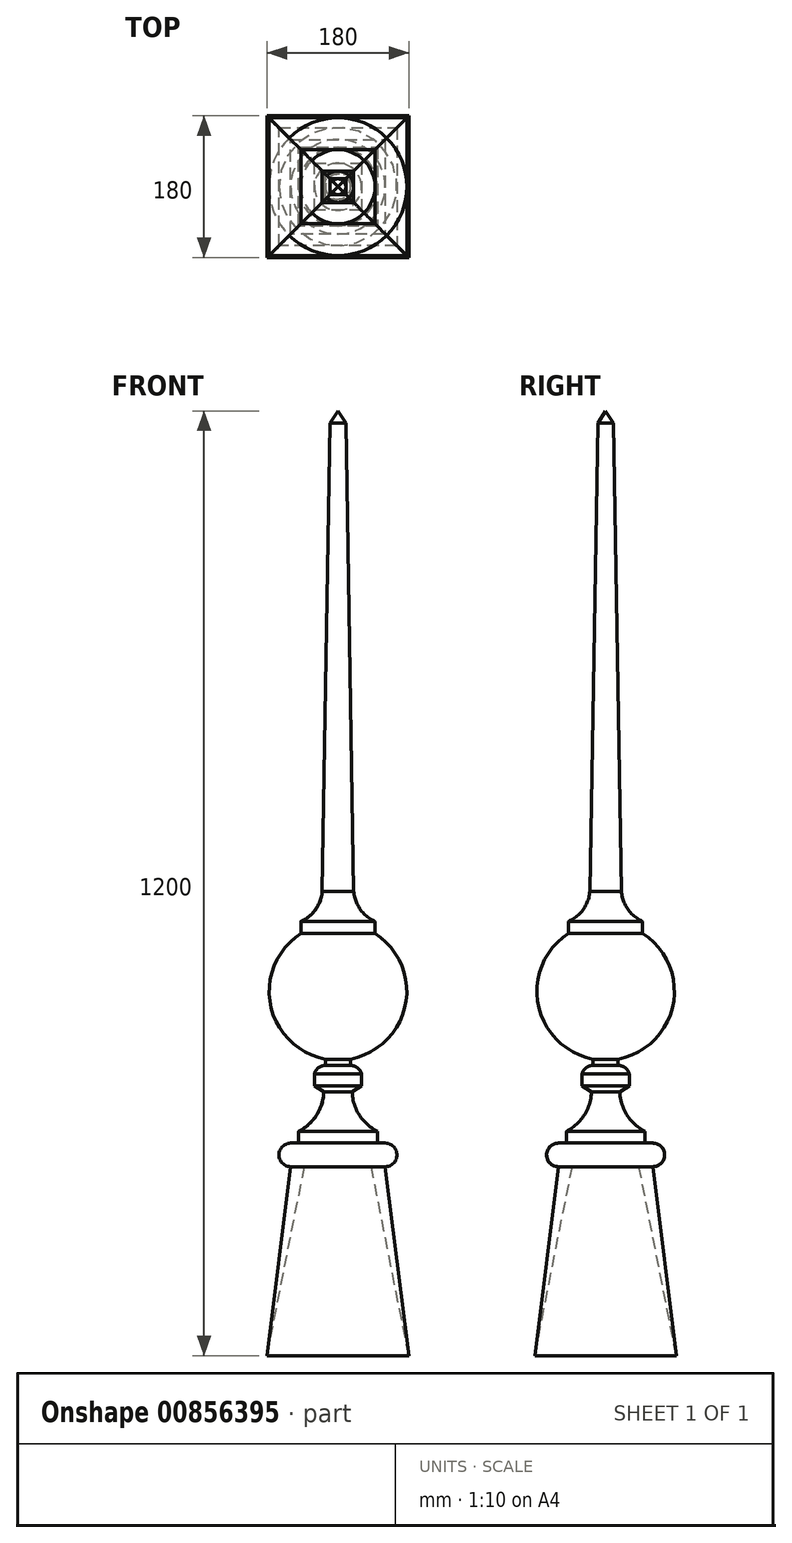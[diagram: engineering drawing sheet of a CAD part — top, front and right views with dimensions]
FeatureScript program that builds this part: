
annotation { "Feature Type Name" : "Feature", "Feature Type Description" : "" }
export const myFeature = defineFeature(function(context is Context, id is Id, definition is map)
    precondition{}
    {
        {
            var Q0;
            Q0=qCreatedBy(makeId("Front.planeOp"),FACE);
            var sketch = newSketch(context, id + "F0", { "sketchPlane" : qUnion([Q0])});
            skLineSegment(sketch, "E0", {"start": v(0, 0) * mm, "end": v(0, 1200) * mm});
            skPoint(sketch, "E1", {"position": v(0, 600) * mm});
            skLineSegment(sketch, "E2", {"start": v(0, 0) * mm, "end": v(90, 0) * mm});
            skLineSegment(sketch, "E3", {"start": v(90, 0) * mm, "end": v(60, 240) * mm});
            skLineSegment(sketch, "E4", {"start": v(60, 240) * mm, "end": v(0, 240) * mm});
            skLineSegment(sketch, "E5", {"start": v(0, 270) * mm, "end": v(60, 270) * mm});
            skArc(sketch, "E6", {"start": v(60, 240) * mm, "mid": v(75, 255) * mm, "end": v(60, 270) * mm});
            skLineSegment(sketch, "E7", {"start": v(50, 270) * mm, "end": v(50, 285) * mm});
            skLineSegment(sketch, "E8", {"start": v(50, 285) * mm, "end": v(0, 285) * mm, "construction": true});
            skLineSegment(sketch, "E9", {"start": v(0, 335) * mm, "end": v(18, 335) * mm, "construction": true});
            skLineSegment(sketch, "E10", {"start": v(18, 335) * mm, "end": v(30, 343) * mm});
            skLineSegment(sketch, "E11", {"start": v(30, 343) * mm, "end": v(30, 358) * mm});
            skLineSegment(sketch, "E12", {"start": v(0, 368.67) * mm, "end": v(16, 368.67) * mm, "construction": true});
            skLineSegment(sketch, "E13", {"start": v(16, 368.67) * mm, "end": v(16, 376.67) * mm});
            skLineSegment(sketch, "E14", {"start": v(16, 376.67) * mm, "end": v(0, 376.67) * mm, "construction": true});
            skArc(sketch, "E15", {"start": v(18, 335) * mm, "mid": v(27.1, 305.59) * mm, "end": v(50, 285) * mm});
            skArc(sketch, "E16", {"start": v(30, 358) * mm, "mid": v(24.8, 365.7) * mm, "end": v(16, 368.67) * mm});
            skLineSegment(sketch, "E17", {"start": v(0, 551.67) * mm, "end": v(46.98, 551.67) * mm});
            skLineSegment(sketch, "E18", {"start": v(46.98, 551.67) * mm, "end": v(46.98, 536.67) * mm});
            skLineSegment(sketch, "E19", {"start": v(46.98, 536.67) * mm, "end": v(0, 536.67) * mm});
            skArc(sketch, "E20", {"start": v(0, 550.33) * mm, "mid": v(-87.57, 462.76) * mm, "end": v(0, 375.2) * mm, "construction": true});
            skArc(sketch, "E21", {"start": v(0, 375.2) * mm, "mid": v(87.57, 462.76) * mm, "end": v(0, 550.33) * mm});
            skLineSegment(sketch, "E22", {"start": v(0, 590) * mm, "end": v(20, 590) * mm});
            skArc(sketch, "E23", {"start": v(20, 590) * mm, "mid": v(28.21, 567.12) * mm, "end": v(46.98, 551.67) * mm});
            skLineSegment(sketch, "E24", {"start": v(0, 1185) * mm, "end": v(10, 1185) * mm});
            skLineSegment(sketch, "E25", {"start": v(10, 1185) * mm, "end": v(20, 590) * mm});
            skLineSegment(sketch, "E26", {"start": v(0, 1200) * mm, "end": v(10, 1185) * mm});
            skSolve(sketch);
        }
        {
            var Q0;
            Q0=qCreatedBy(makeId("Top.planeOp"),FACE);
            var sketch = newSketch(context, id + "F1", { "sketchPlane" : qUnion([Q0])});
            skLineSegment(sketch, "E27.bottom", {"start": v(90, -90) * mm, "end": v(-90, -90) * mm});
            skLineSegment(sketch, "E27.top", {"start": v(90, 90) * mm, "end": v(-90, 90) * mm});
            skLineSegment(sketch, "E27.left", {"start": v(90, -90) * mm, "end": v(90, 90) * mm});
            skLineSegment(sketch, "E27.right", {"start": v(-90, -90) * mm, "end": v(-90, 90) * mm});
            skPoint(sketch, "E27.middle", {"position": v(0, 0) * mm});
            skSolve(sketch);
        }
        {
            var Q0;
            {var subQ0=sQuery(id+"F0.wireOp",EDGE,"E17");Q0=makeQuery(id+"F0.imprint","IMPRINT",FACE,{"disambiguationData":[TD([[makeQuery(id+"F0.imprint","IMPRINT",EDGE,{"derivedFrom":subQ0}),-1.0]])]});}
            var Q1;
            {var subQ5=sQuery(id+"F0.wireOp",EDGE,"E4");Q1=makeQuery(id+"F0.imprint","IMPRINT",FACE,{"disambiguationData":[TD([[makeQuery(id+"F0.imprint","IMPRINT",EDGE,{"derivedFrom":subQ5}),-1.0]])]});}
            var Q2;
            {var subQ2=sQuery(id+"F0.wireOp",EDGE,"E24");Q2=makeQuery(id+"F0.imprint","IMPRINT",FACE,{"disambiguationData":[TD([[makeQuery(id+"F0.imprint","IMPRINT",EDGE,{"derivedFrom":subQ2}),1.0]])]});}
            var Q3;
            {var subQ0=sQuery(id+"F0.wireOp",EDGE,"E19");Q3=makeQuery(id+"F0.imprint","IMPRINT",FACE,{"disambiguationData":[TD([[makeQuery(id+"F0.imprint","IMPRINT",EDGE,{"derivedFrom":subQ0}),-1.0]])]});}
            var Q4;
            {var subQ0=sQuery(id+"F0.wireOp",EDGE,"E22");Q4=makeQuery(id+"F0.imprint","IMPRINT",FACE,{"disambiguationData":[TD([[makeQuery(id+"F0.imprint","IMPRINT",EDGE,{"derivedFrom":subQ0}),1.0]])]});}
            var Q5;
            {var subQ0=sQuery(id+"F0.wireOp",EDGE,"E19");Q5=makeQuery(id+"F0.imprint","IMPRINT",FACE,{"disambiguationData":[TD([[makeQuery(id+"F0.imprint","IMPRINT",EDGE,{"derivedFrom":subQ0}),1.0]])]});}
            var Q6;
            {var subQ0=sQuery(id+"F0.wireOp",EDGE,"E17");Q6=makeQuery(id+"F0.imprint","IMPRINT",FACE,{"disambiguationData":[TD([[makeQuery(id+"F0.imprint","IMPRINT",EDGE,{"derivedFrom":subQ0}),1.0]])]});}
            var Q7;
            {var subQ0=sQuery(id+"F0.wireOp",EDGE,"E7");Q7=makeQuery(id+"F0.imprint","IMPRINT",FACE,{"disambiguationData":[TD([[makeQuery(id+"F0.imprint","IMPRINT",EDGE,{"derivedFrom":subQ0}),1.0]])]});}
            var Q8;
            Q8=sQuery(id+"F0.wireOp",EDGE,"E0");
            revolve(context, id + "F2", {"surfaceOperationType" : NewSurfaceOperationType.NEW, "entities" : qUnion([Q0, Q1, Q2, Q3, Q4, Q5, Q6, Q7]), "axis" : qUnion([Q8]), "revolveType" : RevolveType.FULL});
        }
        {
            var Q1;
            Q1=makeQuery(id+"F1.imprint","IMPRINT",FACE,{"disambiguationData":[TD([[makeQuery(id+"F1.imprint","IMPRINT",EDGE,{"derivedFrom":sQuery(id+"F1.wireOp",EDGE,"E27.bottom")}),-1.0]])]});
            var Q2;
            Q2=makeQuery(id+"F2.opRevolve","SWEPT_FACE",FACE,{"disambiguationData":[OSD([sQuery(id+"F0.wireOp",EDGE,"E4")])]});
            loft(context, id + "F3", {"operationType" : NewBodyOperationType.ADD, "sheetProfilesArray" : [{ "sheetProfileEntities" : qUnion([Q1]) }, { "sheetProfileEntities" : qUnion([Q2]) }]});
        }
        {
            var Q0;
            {var subQ0=sQuery(id+"F0.wireOp",EDGE,"E19");Q0=makeQuery(id+"F0.imprint","IMPRINT",FACE,{"disambiguationData":[TD([[makeQuery(id+"F0.imprint","IMPRINT",EDGE,{"derivedFrom":subQ0}),-1.0]])]});}
            var Q1;
            {var subQ0=sQuery(id+"F0.wireOp",EDGE,"E19");Q1=makeQuery(id+"F0.imprint","IMPRINT",FACE,{"disambiguationData":[TD([[makeQuery(id+"F0.imprint","IMPRINT",EDGE,{"derivedFrom":subQ0}),1.0]])]});}
            var Q2;
            {var subQ0=sQuery(id+"F0.wireOp",EDGE,"E7");Q2=makeQuery(id+"F0.imprint","IMPRINT",FACE,{"disambiguationData":[TD([[makeQuery(id+"F0.imprint","IMPRINT",EDGE,{"derivedFrom":subQ0}),1.0]])]});}
            var Q3;
            {var subQ2=sQuery(id+"F0.wireOp",EDGE,"E24");Q3=makeQuery(id+"F0.imprint","IMPRINT",FACE,{"disambiguationData":[TD([[makeQuery(id+"F0.imprint","IMPRINT",EDGE,{"derivedFrom":subQ2}),1.0]])]});}
            var Q4;
            {var subQ0=sQuery(id+"F0.wireOp",EDGE,"E22");Q4=makeQuery(id+"F0.imprint","IMPRINT",FACE,{"disambiguationData":[TD([[makeQuery(id+"F0.imprint","IMPRINT",EDGE,{"derivedFrom":subQ0}),1.0]])]});}
            var Q5;
            {var subQ0=sQuery(id+"F0.wireOp",EDGE,"E17");Q5=makeQuery(id+"F0.imprint","IMPRINT",FACE,{"disambiguationData":[TD([[makeQuery(id+"F0.imprint","IMPRINT",EDGE,{"derivedFrom":subQ0}),-1.0]])]});}
            var Q6;
            {var subQ5=sQuery(id+"F0.wireOp",EDGE,"E4");Q6=makeQuery(id+"F0.imprint","IMPRINT",FACE,{"disambiguationData":[TD([[makeQuery(id+"F0.imprint","IMPRINT",EDGE,{"derivedFrom":subQ5}),-1.0]])]});}
            var Q7;
            {var subQ0=sQuery(id+"F0.wireOp",EDGE,"E2");Q7=makeQuery(id+"F0.imprint","IMPRINT",FACE,{"disambiguationData":[TD([[makeQuery(id+"F0.imprint","IMPRINT",EDGE,{"derivedFrom":subQ0}),1.0]])]});}
            var Q8;
            {var subQ0=sQuery(id+"F0.wireOp",EDGE,"E17");Q8=makeQuery(id+"F0.imprint","IMPRINT",FACE,{"disambiguationData":[TD([[makeQuery(id+"F0.imprint","IMPRINT",EDGE,{"derivedFrom":subQ0}),1.0]])]});}
            var Q9;
            Q9 = qBodyType(qCreatedBy(id + "F1" ,EDGE), BodyType.WIRE);
            sweep(context, id + "F4", {"profiles" : qUnion([Q0, Q1, Q2, Q3, Q4, Q5, Q6, Q7, Q8]), "path" : qUnion([Q9])});
        }
    });
